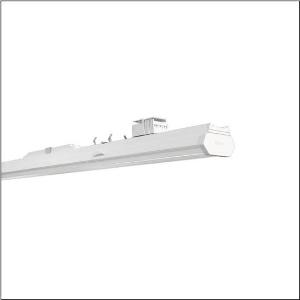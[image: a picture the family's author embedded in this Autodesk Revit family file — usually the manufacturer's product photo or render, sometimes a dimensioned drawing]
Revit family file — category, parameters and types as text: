
# Revit family: licross_11_protected_mo_51tp12cn58xf
name_source: partatom
category: Lighting Fixtures
units: mm (PartAtom-declared; Revit-internal decimal feet)

## family parameters
Cut with Voids When Loaded = No
Host = Face
Light Source = No
Part Type = Normal
Room Calculation Point = No
Round Connector Dimension = Use Diameter
Shared = No

## types (1)
- --- (1 x LED, 8190 lm, 49 W, 5000K)
    Apparent Load = 49 VA
    CIE Flux Codes = 73 92 98 99 100
    Color Rendering = 80
    Color Temperature = 5000K
    Default Elevation = 1800 mm
    Description = Licross 11 Protected MO, luminaire insert, of sheet steel, galvanised, coil coated, white, length: 1.500mm, width: 90mm, height: 101mm, LED rated luminous flux: 8.190lm, light colour: 850, SDCM (Standard Deviation of Colour Matching)MacAdam ≤ 3 SDCM (initial), control gear: ON/OFF Multilumen, CLOi, control gear: ECG Multilumen, with plug, 3-pole, with phase selection, mains connection: 220..240V, AC, 50/60Hz, start of lifetime: 49W, end of service life: 54W, internal wiring halogen-free, primary optical cover: cover, of PMMA, light emission: direct distribution, primary light characteristic: symmetric, protection rating (complete): IP64, insulation class (complete): insulation class I (protective earthing), certification: CE, ENEC, VDE, UKCA, protection symbol: D if used in an environment with conductive dust loads with corresponding accessories, impact resistance: IK06, permissible ambient temperature for indoor applications: -35..+40°C, reducing of maximum allowable ambient temperature of 5°C with ceiling mounting, corresponds to IFS (International Featured Standards) requirements for safety and quality in the food industry, LABS conformity tested according to VDMA 24364:2018-05, The light source and the operating device comply with the requirements of the Ecodesign Regulation (EU) 2019/2020 and are replaceable in accordance with this regulation, packaging unit: 1 piece
    Height = 92 mm
    Lamp = 1 x LED
    Lamp Light Flux = 8190 lm
    Lamp Power = 49 W
    Lamp count = 1
    Length = 1500 mm
    Luminous efficacy = 167 lm/W
    Manufacturer = Siteco
    ModVariant = No
    Model = 51TP12CN58XF
    Mounting Place = Ceiling
    Mounting Type = Pendant
    Number of Poles = 1
    OnlyDefault = Yes
    Power Factor = 1
    Product Name = Licross 11 Protected MO
    Product group = luminaire insert | ceiling pendant
    ProductGroupID = 901
    Protection Class = Protection class I
    Protection Degree = IP 64
    RLX_Detail_Level = 1
    RLX_Emergency_Light_Flux = 0 lm
    RLX_Emergency_Type = 0
    RLX_Emergency_Type_DB = No
    RlxData = <blob elided: 22445 chars, md5=f657d975>
    Socket = socket
    Standby Power = 0 W
    System Light Flux = 8190 lm
    System Power = 49 W
    Type Comments = factory setting: luminous flux: 100 % | (A | C | E) | 111 mA
    Type Image = l_1256148.jpg
    URL = http://relux.com
    VarID = @adj_197519
    Voltage = 0 V
    Weight = 0.00 kg
    Width = 88 mm

## geometry (parser evidence)
native form markers: Blend x4, Sweep x10
no freeform markers — native parametric forms only
